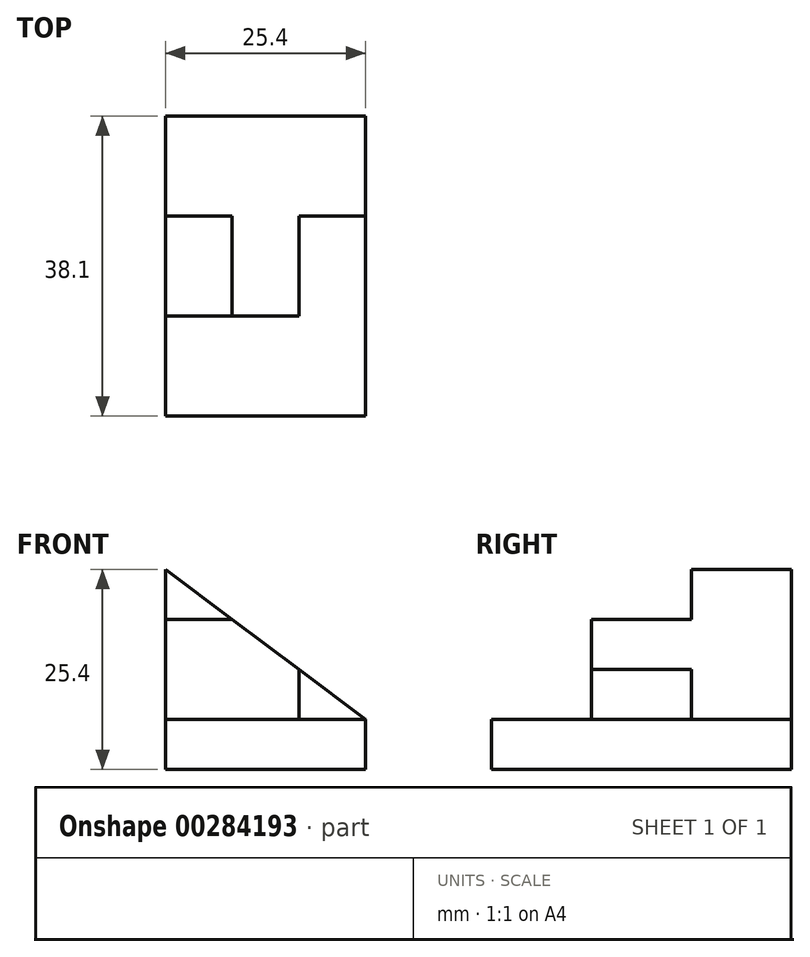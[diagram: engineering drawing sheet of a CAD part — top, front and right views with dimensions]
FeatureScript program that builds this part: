
annotation { "Feature Type Name" : "Feature", "Feature Type Description" : "" }
export const myFeature = defineFeature(function(context is Context, id is Id, definition is map)
    precondition{}
    {
        {
            var Q0;
            Q0=qCreatedBy(makeId("Front.planeOp"),FACE);
            var sketch = newSketch(context, id + "F0", { "sketchPlane" : qUnion([Q0])});
            skLineSegment(sketch, "E0", {"start": v(0, 0) * mm, "end": v(0, 25.4) * mm});
            skLineSegment(sketch, "E1", {"start": v(0, 0) * mm, "end": v(25.4, 0) * mm});
            skLineSegment(sketch, "E2", {"start": v(25.4, 0) * mm, "end": v(25.4, 6.35) * mm});
            skLineSegment(sketch, "E3", {"start": v(25.4, 6.35) * mm, "end": v(0, 25.4) * mm});
            skSolve(sketch);
        }
        {
            var Q0;
            Q0=makeQuery(id+"F0.imprint","IMPRINT",FACE,{"disambiguationData":[TD([[makeQuery(id+"F0.imprint","IMPRINT",EDGE,{"derivedFrom":sQuery(id+"F0.wireOp",EDGE,"E0")}),-1.0]])]});
            extrude(context, id + "F1", {"entities" : qUnion([Q0]), "endBound" : BoundingType.SYMMETRIC, "depth" : 38.1 * mm});
        }
        {
            var Q0;
            Q0=makeQuery(id+"F1.opExtrude","CAP_FACE",FACE,{"disambiguationData":[OSD([sQuery(id+"F0.wireOp",EDGE,"E0"),sQuery(id+"F0.wireOp",EDGE,"E1"),sQuery(id+"F0.wireOp",EDGE,"E2"),sQuery(id+"F0.wireOp",EDGE,"E3")])],"isStart":false});
            var sketch = newSketch(context, id + "F2", { "sketchPlane" : qUnion([Q0])});
            skLineSegment(sketch, "E4", {"start": v(25.4, 6.35) * mm, "end": v(0, 6.35) * mm});
            skPoint(sketch, "E4.endSnap0", {"position": v(0, 12.7) * mm});
            skSolve(sketch);
        }
        {
            var Q0;
            {var subQ0=sQuery(id+"F2.wireOp",EDGE,"E4");Q0=makeQuery(id+"F2.imprint","IMPRINT",FACE,{"disambiguationData":[TD([[makeQuery(id+"F2.imprint","IMPRINT",EDGE,{"derivedFrom":subQ0}),-1.0]])]});}
            extrude(context, id + "F3", {"entities" : qUnion([Q0]), "operationType" : NewBodyOperationType.REMOVE, "oppositeDirection" : true, "depth" : 12.7 * mm});
        }
        {
            var Q0;
            Q0=makeQuery(id+"F3.boolean.opBoolean","COPY",FACE,{"derivedFrom":makeQuery(id+"F3.opExtrude","CAP_FACE",FACE,{"disambiguationData":[OSD([sQuery(id+"F0.wireOp",EDGE,"E0"),sQuery(id+"F0.wireOp",EDGE,"E3"),sQuery(id+"F2.wireOp",EDGE,"E4")])],"isStart":false})});
            var sketch = newSketch(context, id + "F4", { "sketchPlane" : qUnion([Q0])});
            skLineSegment(sketch, "E5", {"start": v(0, 25.4) * mm, "end": v(0, 19.05) * mm});
            skLineSegment(sketch, "E6", {"start": v(0, 19.05) * mm, "end": v(8.47, 19.05) * mm});
            skSolve(sketch);
        }
        {
            var Q0;
            {var subQ0=sQuery(id+"F4.wireOp",EDGE,"E5");Q0=makeQuery(id+"F4.imprint","IMPRINT",FACE,{"disambiguationData":[TD([[makeQuery(id+"F4.imprint","IMPRINT",EDGE,{"derivedFrom":subQ0}),-1.0]])]});}
            extrude(context, id + "F5", {"entities" : qUnion([Q0]), "operationType" : NewBodyOperationType.REMOVE, "oppositeDirection" : true, "depth" : 12.7 * mm});
        }
        {
            var Q0;
            Q0=makeQuery(id+"F3.boolean.opBoolean","COPY",FACE,{"derivedFrom":makeQuery(id+"F3.opExtrude","CAP_FACE",FACE,{"disambiguationData":[OSD([sQuery(id+"F0.wireOp",EDGE,"E0"),sQuery(id+"F0.wireOp",EDGE,"E3"),sQuery(id+"F2.wireOp",EDGE,"E4")])],"isStart":false})});
            var sketch = newSketch(context, id + "F6", { "sketchPlane" : qUnion([Q0])});
            skLineSegment(sketch, "E7", {"start": v(16.93, 12.7) * mm, "end": v(16.93, 6.35) * mm});
            skLineSegment(sketch, "E8", {"start": v(16.93, 6.35) * mm, "end": v(25.4, 6.35) * mm});
            skLineSegment(sketch, "E9", {"start": v(25.4, 6.35) * mm, "end": v(16.93, 12.7) * mm});
            skSolve(sketch);
        }
        {
            var Q0;
            Q0=makeQuery(id+"F6.imprint","IMPRINT",FACE,{"disambiguationData":[TD([[makeQuery(id+"F6.imprint","IMPRINT",EDGE,{"derivedFrom":sQuery(id+"F6.wireOp",EDGE,"E7")}),1.0]])]});
            extrude(context, id + "F7", {"entities" : qUnion([Q0]), "operationType" : NewBodyOperationType.REMOVE, "oppositeDirection" : true, "depth" : 12.7 * mm});
        }
    });
